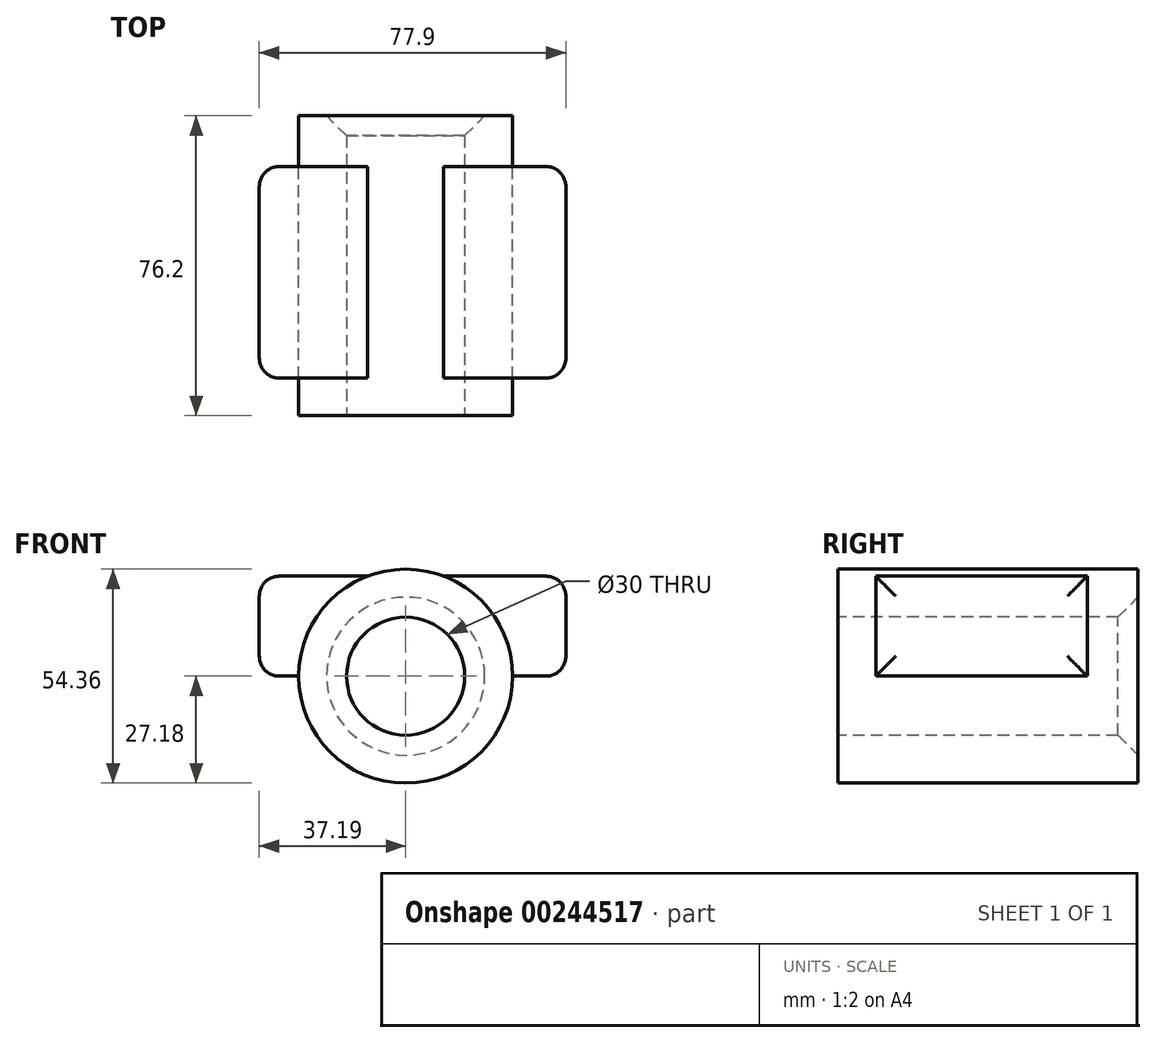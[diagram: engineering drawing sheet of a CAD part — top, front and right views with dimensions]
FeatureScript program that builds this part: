
annotation { "Feature Type Name" : "Feature", "Feature Type Description" : "" }
export const myFeature = defineFeature(function(context is Context, id is Id, definition is map)
    precondition{}
    {
        {
            var Q0;
            Q0=qCreatedBy(makeId("Front.planeOp"),FACE);
            var sketch = newSketch(context, id + "F0", { "sketchPlane" : qUnion([Q0])});
            skCircle(sketch, "E0", {"center": v(0, 0) * mm, "radius": 27.18 * mm});
            skSolve(sketch);
        }
        {
            var Q0;
            Q0=qCreatedBy(makeId("Top.planeOp"),FACE);
            var sketch = newSketch(context, id + "F1", { "sketchPlane" : qUnion([Q0])});
            skLineSegment(sketch, "E1.bottom", {"start": v(-37.19, 25.2) * mm, "end": v(40.7, 25.2) * mm});
            skLineSegment(sketch, "E1.top", {"start": v(-37.19, -28.55) * mm, "end": v(40.7, -28.55) * mm});
            skLineSegment(sketch, "E1.left", {"start": v(-37.19, 25.2) * mm, "end": v(-37.19, -28.55) * mm});
            skLineSegment(sketch, "E1.right", {"start": v(40.7, 25.2) * mm, "end": v(40.7, -28.55) * mm});
            skSolve(sketch);
        }
        {
            var Q0;
            Q0 = qSketchRegion(id + "F1", true);
            extrude(context, id + "F2", {"entities" : qUnion([Q0]), "depth" : 25.4 * mm});
        }
        {
            var Q0;
            Q0 = qSketchRegion(id + "F0", true);
            extrude(context, id + "F3", {"entities" : qUnion([Q0]), "operationType" : NewBodyOperationType.ADD, "endBound" : BoundingType.SYMMETRIC, "depth" : 76.2 * mm});
        }
        {
            var Q0;
            Q0=makeQuery(id+"F2.opExtrude","SWEPT_FACE",FACE,{"disambiguationData":[OSD([sQuery(id+"F1.wireOp",EDGE,"E1.right")])]});
            var Q1;
            Q1=makeQuery(id+"F2.opExtrude","SWEPT_FACE",FACE,{"disambiguationData":[OSD([sQuery(id+"F1.wireOp",EDGE,"E1.left")])]});
            fillet(context, id + "F4", {"entities" : qUnion([Q0, Q1]), "radius" : 5.08 * mm, "tangentPropagation" : true, "allowEdgeOverflow" : false});
        }
        {
            var Q0;
            Q0=makeQuery(id+"F3.opExtrude","CAP_FACE",FACE,{"disambiguationData":[OSD([sQuery(id+"F0.wireOp",EDGE,"E0")])],"isStart":false});
            var sketch = newSketch(context, id + "F5", { "sketchPlane" : qUnion([Q0])});
            skCircle(sketch, "E2", {"center": v(0, 0) * mm, "radius": 15 * mm});
            skSolve(sketch);
        }
        {
            var Q0;
            Q0 = qSketchRegion(id + "F5", true);
            extrude(context, id + "F6", {"entities" : qUnion([Q0]), "operationType" : NewBodyOperationType.REMOVE, "endBound" : BoundingType.THROUGH_ALL, "oppositeDirection" : true, "depth" : 25.4 * mm});
        }
        {
            var Q0;
            Q0=makeQuery(id+"F6.boolean.opBoolean","COPY",EDGE,{"derivedFrom":makeQuery(id+"F6.opExtrude","CAP_EDGE",EDGE,{"disambiguationData":[OSD([sQuery(id+"F5.wireOp",EDGE,"E2")])],"isStart":true})});
            var Q1;
            Q1=makeQuery(id+"F6.boolean.opBoolean","INTERSECT",EDGE,{"derivedFrom":[makeQuery(id+"F3.opExtrude","CAP_FACE",FACE,{"disambiguationData":[OSD([sQuery(id+"F0.wireOp",EDGE,"E0")])],"isStart":true}),makeQuery(id+"F6.opExtrude","SWEPT_FACE",FACE,{"disambiguationData":[OSD([sQuery(id+"F5.wireOp",EDGE,"E2")])]})]});
            chamfer(context, id + "F7", {"entities" : qUnion([Q0, Q1]), "width" : 5.08 * mm, "tangentPropagation" : true});
        }
    });
